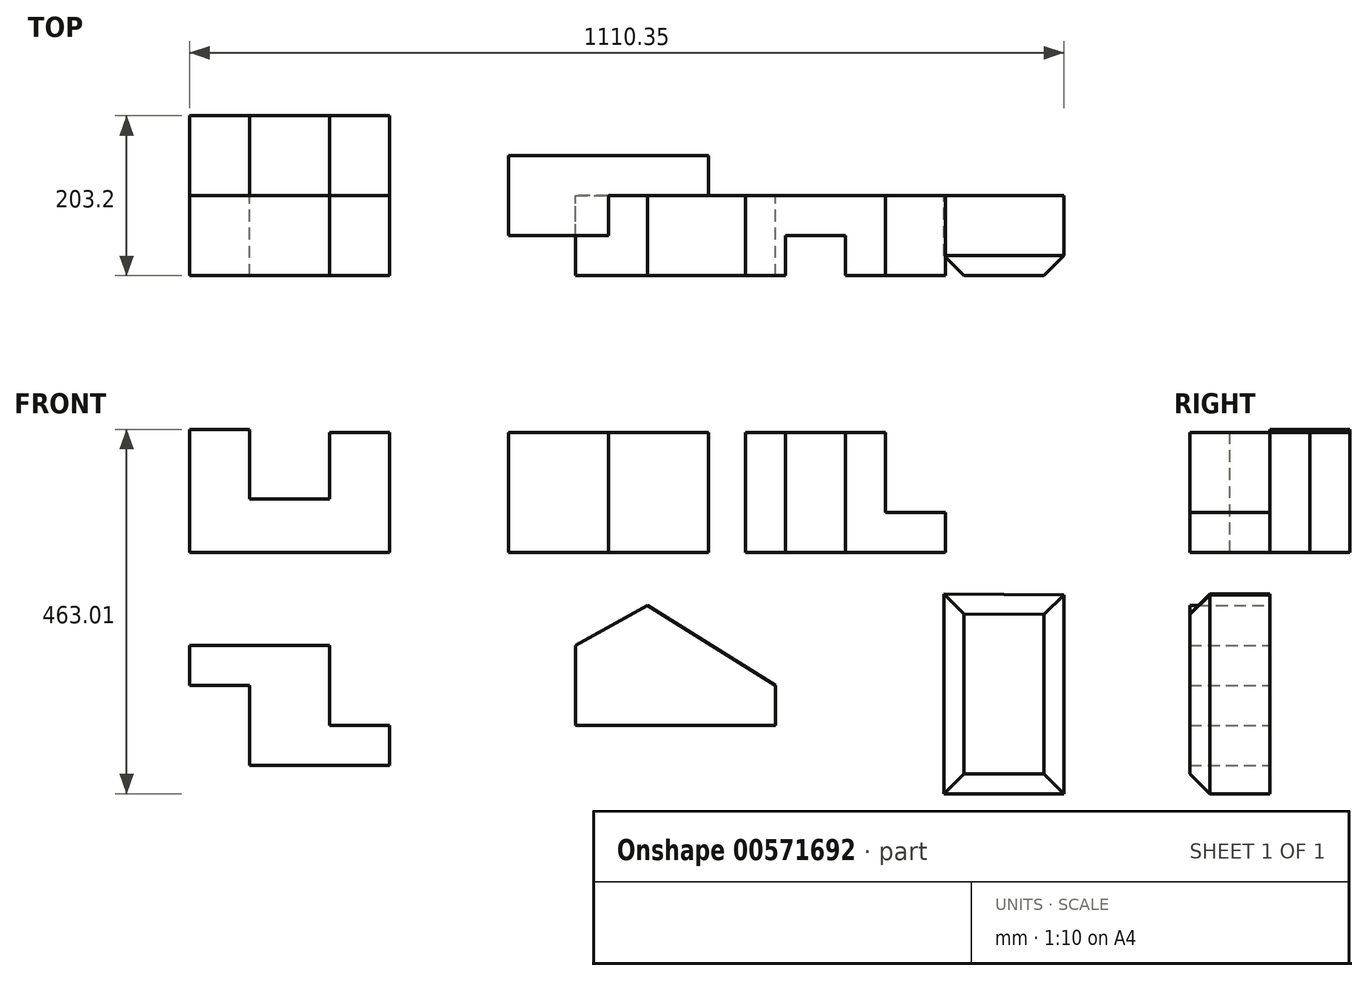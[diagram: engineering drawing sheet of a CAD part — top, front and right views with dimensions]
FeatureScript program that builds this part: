
annotation { "Feature Type Name" : "Feature", "Feature Type Description" : "" }
export const myFeature = defineFeature(function(context is Context, id is Id, definition is map)
    precondition{}
    {
        {
            var Q0;
            Q0=qCreatedBy(makeId("Front.planeOp"),FACE);
            var sketch = newSketch(context, id + "F0", { "sketchPlane" : qUnion([Q0])});
            skLineSegment(sketch, "E0", {"start": v(0, 0) * mm, "end": v(0, 156.5) * mm});
            skLineSegment(sketch, "E1", {"start": v(0, 156.5) * mm, "end": v(76.2, 156.5) * mm});
            skLineSegment(sketch, "E2", {"start": v(76.2, 156.5) * mm, "end": v(76.2, 68) * mm});
            skLineSegment(sketch, "E3", {"start": v(76.2, 68) * mm, "end": v(177.8, 68) * mm});
            skLineSegment(sketch, "E4", {"start": v(177.8, 68) * mm, "end": v(177.8, 152.4) * mm});
            skLineSegment(sketch, "E5", {"start": v(177.8, 152.4) * mm, "end": v(254, 152.4) * mm});
            skLineSegment(sketch, "E6", {"start": v(254, 152.4) * mm, "end": v(254, 0) * mm});
            skLineSegment(sketch, "E7", {"start": v(254, 0) * mm, "end": v(0, 0) * mm});
            skSolve(sketch);
        }
        {
            var Q0;
            Q0=makeQuery(id+"F0.imprint","IMPRINT",FACE,{"disambiguationData":[TD([[makeQuery(id+"F0.imprint","IMPRINT",EDGE,{"derivedFrom":sQuery(id+"F0.wireOp",EDGE,"E0")}),-1.0]])]});
            extrude(context, id + "F1", {"entities" : qUnion([Q0]), "oppositeDirection" : true, "depth" : 101.6 * mm, "offsetDistance" : 25.4 * mm});
        }
        {
            var Q0;
            Q0=qCreatedBy(makeId("Front.planeOp"),FACE);
            var sketch = newSketch(context, id + "F2", { "sketchPlane" : qUnion([Q0])});
            skLineSegment(sketch, "E8", {"start": v(404.82, 0) * mm, "end": v(404.82, 152.4) * mm});
            skLineSegment(sketch, "E9", {"start": v(404.82, 152.4) * mm, "end": v(658.82, 152.4) * mm});
            skLineSegment(sketch, "E10", {"start": v(658.82, 152.4) * mm, "end": v(658.82, 0) * mm});
            skLineSegment(sketch, "E11", {"start": v(658.82, 0) * mm, "end": v(404.82, 0) * mm});
            skSolve(sketch);
        }
        {
            var Q0;
            Q0=makeQuery(id+"F2.imprint","IMPRINT",FACE,{"disambiguationData":[TD([[makeQuery(id+"F2.imprint","IMPRINT",EDGE,{"derivedFrom":sQuery(id+"F2.wireOp",EDGE,"E8")}),-1.0]])]});
            extrude(context, id + "F3", {"entities" : qUnion([Q0]), "oppositeDirection" : true, "depth" : 50.8 * mm, "offsetDistance" : 25.4 * mm});
        }
        {
            var Q0;
            Q0=makeQuery(id+"F3.opExtrude","CAP_FACE",FACE,{"disambiguationData":[OSD([sQuery(id+"F2.wireOp",EDGE,"E8"),sQuery(id+"F2.wireOp",EDGE,"E9"),sQuery(id+"F2.wireOp",EDGE,"E10"),sQuery(id+"F2.wireOp",EDGE,"E11")])],"isStart":true});
            var sketch = newSketch(context, id + "F4", { "sketchPlane" : qUnion([Q0])});
            skLineSegment(sketch, "E12", {"start": v(404.82, 152.4) * mm, "end": v(531.82, 152.4) * mm});
            skLineSegment(sketch, "E13", {"start": v(531.82, 152.4) * mm, "end": v(531.82, 0) * mm});
            skLineSegment(sketch, "E14", {"start": v(531.82, 0) * mm, "end": v(404.82, 0) * mm});
            skLineSegment(sketch, "E15", {"start": v(404.82, 0) * mm, "end": v(404.82, 152.4) * mm});
            skSolve(sketch);
        }
        {
            var Q0;
            Q0 = qSketchRegion(id + "F4", true);
            extrude(context, id + "F5", {"entities" : qUnion([Q0]), "operationType" : NewBodyOperationType.ADD, "depth" : 50.8 * mm, "offsetDistance" : 25.4 * mm});
        }
        {
            var Q0;
            Q0=qCreatedBy(makeId("Front.planeOp"),FACE);
            var sketch = newSketch(context, id + "F6", { "sketchPlane" : qUnion([Q0])});
            skLineSegment(sketch, "E16", {"start": v(705.8, 0) * mm, "end": v(705.8, 152.4) * mm});
            skLineSegment(sketch, "E17", {"start": v(705.8, 152.4) * mm, "end": v(883.6, 152.4) * mm});
            skLineSegment(sketch, "E18", {"start": v(883.6, 152.4) * mm, "end": v(883.6, 50.8) * mm});
            skLineSegment(sketch, "E19", {"start": v(883.6, 50.8) * mm, "end": v(959.8, 50.8) * mm});
            skLineSegment(sketch, "E20", {"start": v(959.8, 50.8) * mm, "end": v(959.8, 0) * mm});
            skLineSegment(sketch, "E21", {"start": v(959.8, 0) * mm, "end": v(705.8, 0) * mm});
            skSolve(sketch);
        }
        {
            var Q0;
            Q0 = qSketchRegion(id + "F6", true);
            extrude(context, id + "F7", {"entities" : qUnion([Q0]), "depth" : 101.6 * mm, "offsetDistance" : 25.4 * mm});
        }
        {
            var Q0;
            Q0=makeQuery(id+"F7.opExtrude","SWEPT_FACE",FACE,{"disambiguationData":[OSD([sQuery(id+"F6.wireOp",EDGE,"E17")])]});
            var sketch = newSketch(context, id + "F8", { "sketchPlane" : qUnion([Q0])});
            skLineSegment(sketch, "E22", {"start": v(756.6, -101.6) * mm, "end": v(756.6, -50.8) * mm});
            skLineSegment(sketch, "E23", {"start": v(756.6, -50.8) * mm, "end": v(832.8, -50.8) * mm});
            skLineSegment(sketch, "E24", {"start": v(832.8, -50.8) * mm, "end": v(832.8, -101.6) * mm});
            skLineSegment(sketch, "E25", {"start": v(832.8, -101.6) * mm, "end": v(756.6, -101.6) * mm});
            skSolve(sketch);
        }
        {
            var Q0;
            Q0 = qSketchRegion(id + "F8", true);
            extrude(context, id + "F9", {"entities" : qUnion([Q0]), "operationType" : NewBodyOperationType.REMOVE, "oppositeDirection" : true, "depth" : 152.4 * mm, "offsetDistance" : 25.4 * mm});
        }
        {
            var Q0;
            Q0=qCreatedBy(makeId("Front.planeOp"),FACE);
            var sketch = newSketch(context, id + "F10", { "sketchPlane" : qUnion([Q0])});
            skLineSegment(sketch, "E26", {"start": v(0, -118.34) * mm, "end": v(0, -169.14) * mm});
            skLineSegment(sketch, "E27", {"start": v(0, -169.14) * mm, "end": v(76.2, -169.14) * mm});
            skLineSegment(sketch, "E28", {"start": v(76.2, -169.14) * mm, "end": v(76.2, -270.74) * mm});
            skLineSegment(sketch, "E29", {"start": v(76.2, -270.74) * mm, "end": v(254, -270.74) * mm});
            skLineSegment(sketch, "E30", {"start": v(254, -270.74) * mm, "end": v(254, -219.94) * mm});
            skLineSegment(sketch, "E31", {"start": v(254, -219.94) * mm, "end": v(177.8, -219.94) * mm});
            skLineSegment(sketch, "E32", {"start": v(177.8, -219.94) * mm, "end": v(177.8, -118.34) * mm});
            skLineSegment(sketch, "E33", {"start": v(177.8, -118.34) * mm, "end": v(0, -118.34) * mm});
            skSolve(sketch);
        }
        {
            var Q0;
            Q0 = qSketchRegion(id + "F10", true);
            extrude(context, id + "F11", {"entities" : qUnion([Q0]), "depth" : 101.6 * mm, "offsetDistance" : 25.4 * mm});
        }
        {
            var Q0;
            Q0=qCreatedBy(makeId("Front.planeOp"),FACE);
            var sketch = newSketch(context, id + "F12", { "sketchPlane" : qUnion([Q0])});
            skLineSegment(sketch, "E34", {"start": v(490.37, -118.39) * mm, "end": v(490.37, -219.99) * mm});
            skLineSegment(sketch, "E35", {"start": v(490.37, -219.99) * mm, "end": v(744.37, -219.99) * mm});
            skLineSegment(sketch, "E36", {"start": v(744.37, -219.99) * mm, "end": v(744.37, -169.19) * mm});
            skLineSegment(sketch, "E37", {"start": v(744.37, -169.19) * mm, "end": v(581.64, -67.59) * mm});
            skLineSegment(sketch, "E38", {"start": v(581.64, -67.59) * mm, "end": v(490.37, -118.39) * mm});
            skSolve(sketch);
        }
        {
            var Q0;
            Q0=makeQuery(id+"F12.imprint","IMPRINT",FACE,{"disambiguationData":[TD([[makeQuery(id+"F12.imprint","IMPRINT",EDGE,{"derivedFrom":sQuery(id+"F12.wireOp",EDGE,"E34")}),1.0]])]});
            extrude(context, id + "F13", {"entities" : qUnion([Q0]), "depth" : 101.6 * mm, "offsetDistance" : 25.4 * mm});
        }
        {
            var Q0;
            Q0=qCreatedBy(makeId("Front.planeOp"),FACE);
            var sketch = newSketch(context, id + "F14", { "sketchPlane" : qUnion([Q0])});
            skLineSegment(sketch, "E39", {"start": v(957.95, -52.51) * mm, "end": v(957.95, -306.51) * mm});
            skLineSegment(sketch, "E40", {"start": v(957.95, -306.51) * mm, "end": v(1110.35, -306.51) * mm});
            skLineSegment(sketch, "E41", {"start": v(1110.35, -306.51) * mm, "end": v(1110.35, -53.71) * mm});
            skLineSegment(sketch, "E42", {"start": v(1110.35, -53.71) * mm, "end": v(957.95, -52.51) * mm});
            skSolve(sketch);
        }
        {
            var Q0;
            Q0 = qSketchRegion(id + "F14", true);
            extrude(context, id + "F15", {"entities" : qUnion([Q0]), "depth" : 101.6 * mm, "offsetDistance" : 25.4 * mm});
        }
        {
            var Q0;
            Q0=makeQuery(id+"F15.opExtrude","CAP_FACE",FACE,{"disambiguationData":[OSD([sQuery(id+"F14.wireOp",EDGE,"E39"),sQuery(id+"F14.wireOp",EDGE,"E40"),sQuery(id+"F14.wireOp",EDGE,"E41"),sQuery(id+"F14.wireOp",EDGE,"E42")])],"isStart":false});
            chamfer(context, id + "F16", {"entities" : qUnion([Q0]), "width" : 25.4 * mm, "tangentPropagation" : true});
        }
    });
